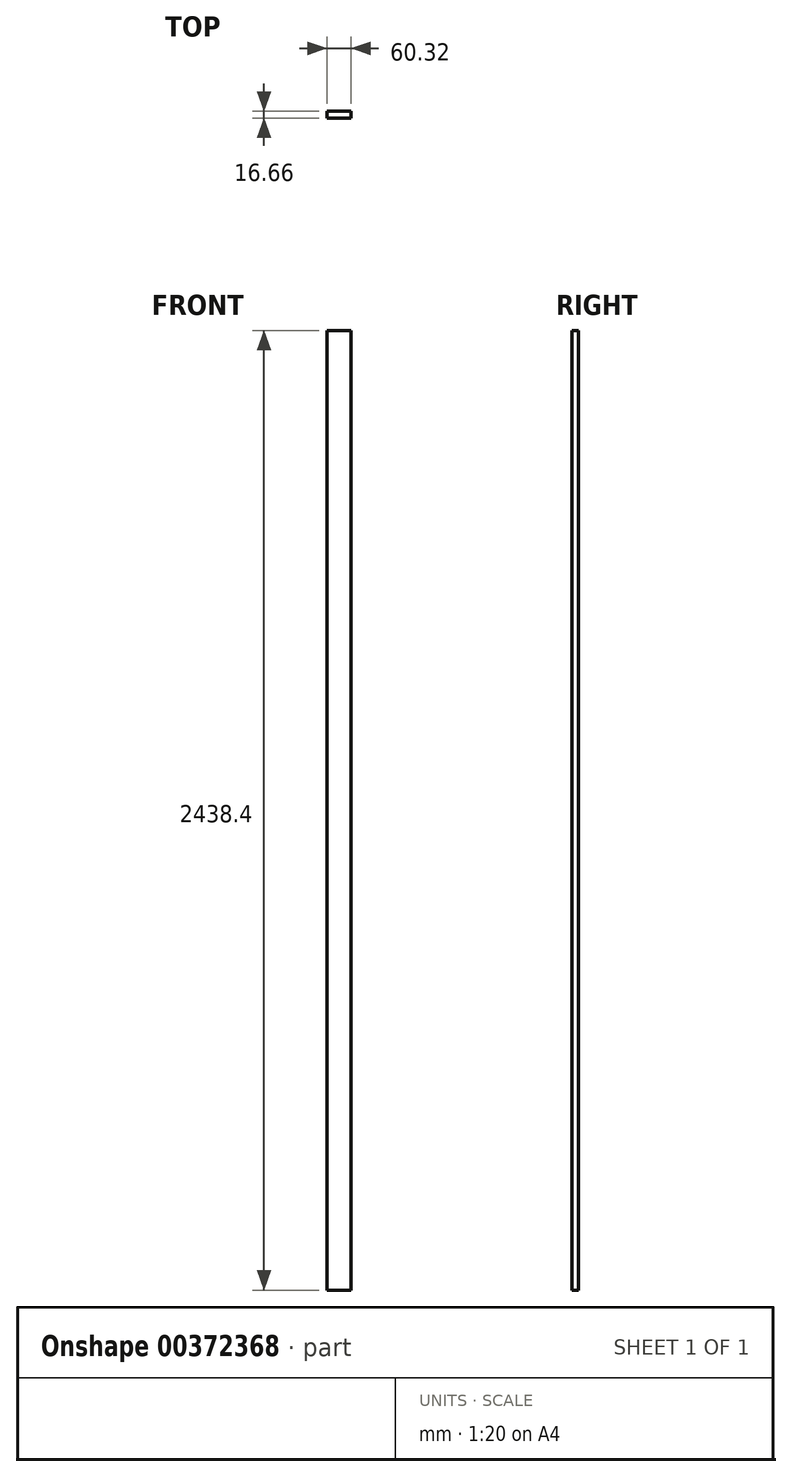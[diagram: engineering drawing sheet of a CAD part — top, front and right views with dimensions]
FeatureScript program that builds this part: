
annotation { "Feature Type Name" : "Feature", "Feature Type Description" : "" }
export const myFeature = defineFeature(function(context is Context, id is Id, definition is map)
    precondition{}
    {
        {
            var Q0;
            Q0=qCreatedBy(makeId("Top.planeOp"),FACE);
            var sketch = newSketch(context, id + "F0", { "sketchPlane" : qUnion([Q0])});
            skLineSegment(sketch, "E0.bottom", {"start": v(-30.16, 8.33) * mm, "end": v(30.16, 8.33) * mm});
            skLineSegment(sketch, "E0.top", {"start": v(-30.16, -8.33) * mm, "end": v(30.16, -8.33) * mm});
            skLineSegment(sketch, "E0.left", {"start": v(-30.16, 8.33) * mm, "end": v(-30.16, -8.33) * mm});
            skLineSegment(sketch, "E0.right", {"start": v(30.16, 8.33) * mm, "end": v(30.16, -8.33) * mm});
            skPoint(sketch, "E0.middle", {"position": v(0, 0) * mm});
            skSolve(sketch);
        }
        {
            var Q0;
            Q0=makeQuery(id+"F0.imprint","IMPRINT",FACE,{"disambiguationData":[TD([[makeQuery(id+"F0.imprint","IMPRINT",EDGE,{"derivedFrom":sQuery(id+"F0.wireOp",EDGE,"E0.bottom")}),-1.0]])]});
            extrude(context, id + "F1", {"entities" : qUnion([Q0]), "endBound" : BoundingType.SYMMETRIC, "depth" : 2438.4 * mm});
        }
    });
